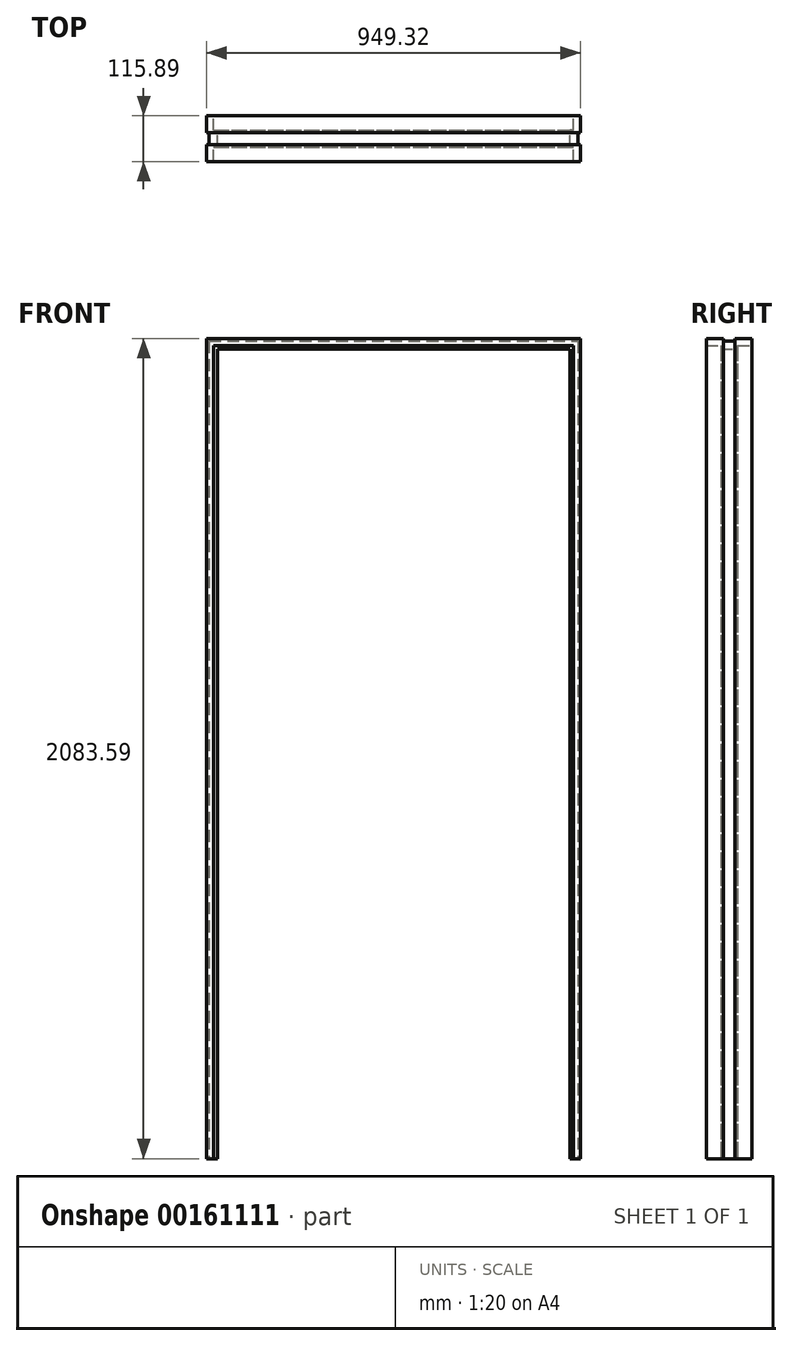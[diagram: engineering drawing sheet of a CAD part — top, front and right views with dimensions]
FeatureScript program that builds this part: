
annotation { "Feature Type Name" : "Feature", "Feature Type Description" : "" }
export const myFeature = defineFeature(function(context is Context, id is Id, definition is map)
    precondition{}
    {
        {
            var Q0;
            Q0=qCreatedBy(makeId("Top.planeOp"),FACE);
            var sketch = newSketch(context, id + "F0", { "sketchPlane" : qUnion([Q0])});
            skLineSegment(sketch, "E0", {"start": v(0, 115.89) * mm, "end": v(-17.46, 115.89) * mm});
            skLineSegment(sketch, "E1", {"start": v(-17.46, 115.89) * mm, "end": v(-17.46, 79.38) * mm});
            skLineSegment(sketch, "E2", {"start": v(-17.46, 79.38) * mm, "end": v(-26.99, 79.38) * mm});
            skLineSegment(sketch, "E3", {"start": v(-26.99, 79.38) * mm, "end": v(-26.99, 36.51) * mm});
            skLineSegment(sketch, "E4", {"start": v(-26.99, 36.51) * mm, "end": v(-17.46, 36.51) * mm});
            skLineSegment(sketch, "E5", {"start": v(-17.46, 36.51) * mm, "end": v(-17.46, 0) * mm});
            skLineSegment(sketch, "E6", {"start": v(-17.46, 0) * mm, "end": v(0, 0) * mm});
            skLineSegment(sketch, "E7", {"start": v(-474.66, 0) * mm, "end": v(-474.66, 102.45) * mm, "construction": true});
            skLineSegment(sketch, "E8.bottom", {"start": v(0, 73.03) * mm, "end": v(-6.35, 73.03) * mm});
            skLineSegment(sketch, "E8.top", {"start": v(0, 42.86) * mm, "end": v(-6.35, 42.86) * mm});
            skLineSegment(sketch, "E8.right", {"start": v(-6.35, 73.03) * mm, "end": v(-6.35, 42.86) * mm});
            skLineSegment(sketch, "E9", {"start": v(0, 115.89) * mm, "end": v(0, 73.03) * mm});
            skLineSegment(sketch, "E10", {"start": v(0, 42.86) * mm, "end": v(0, 0) * mm});
            skLineSegment(sketch, "E11.MirrorCS", {"start": v(-949.33, 73.03) * mm, "end": v(-942.98, 73.03) * mm});
            skLineSegment(sketch, "E12.MirrorCS", {"start": v(-949.33, 42.86) * mm, "end": v(-942.98, 42.86) * mm});
            skLineSegment(sketch, "E13.MirrorCS", {"start": v(-949.33, 115.89) * mm, "end": v(-931.86, 115.89) * mm});
            skLineSegment(sketch, "E14.MirrorCS", {"start": v(-931.86, 0) * mm, "end": v(-949.33, 0) * mm});
            skLineSegment(sketch, "E15.MirrorCS", {"start": v(-931.86, 79.38) * mm, "end": v(-922.34, 79.38) * mm});
            skLineSegment(sketch, "E16.MirrorCS", {"start": v(-922.34, 36.51) * mm, "end": v(-931.86, 36.51) * mm});
            skLineSegment(sketch, "E17.MirrorCS", {"start": v(-949.33, 42.86) * mm, "end": v(-949.33, 0) * mm});
            skLineSegment(sketch, "E18.MirrorCS", {"start": v(-949.33, 115.89) * mm, "end": v(-949.33, 73.03) * mm});
            skLineSegment(sketch, "E19.MirrorCS", {"start": v(-922.34, 79.38) * mm, "end": v(-922.34, 36.51) * mm});
            skLineSegment(sketch, "E20.MirrorCS", {"start": v(-931.86, 115.89) * mm, "end": v(-931.86, 79.38) * mm});
            skLineSegment(sketch, "E21.MirrorCS", {"start": v(-942.98, 73.03) * mm, "end": v(-942.98, 42.86) * mm});
            skLineSegment(sketch, "E22.MirrorCS", {"start": v(-931.86, 36.51) * mm, "end": v(-931.86, 0) * mm});
            skSolve(sketch);
        }
        {
            var Q0;
            Q0 = qSketchRegion(id + "F0", true);
            extrude(context, id + "F1", {"entities" : qUnion([Q0]), "depth" : 2083.6 * mm});
        }
        {
            var Q0;
            Q0=qCreatedBy(makeId("Front.planeOp"),FACE);
            var sketch = newSketch(context, id + "F2", { "sketchPlane" : qUnion([Q0])});
            skPoint(sketch, "E23.0", {"position": v(-949.33, 2083.6) * mm});
            skPoint(sketch, "E24.0", {"position": v(0, 2083.6) * mm});
            skLineSegment(sketch, "E25", {"start": v(-949.33, 2083.6) * mm, "end": v(-474.66, 1608.93) * mm});
            skLineSegment(sketch, "E26", {"start": v(-474.66, 1608.93) * mm, "end": v(0, 2083.6) * mm});
            skLineSegment(sketch, "E27", {"start": v(-949.33, 2083.6) * mm, "end": v(0, 2083.6) * mm});
            skSolve(sketch);
        }
        {
            var Q0;
            Q0 = qSketchRegion(id + "F2", true);
            extrude(context, id + "F3", {"entities" : qUnion([Q0]), "operationType" : NewBodyOperationType.REMOVE, "endBound" : BoundingType.THROUGH_ALL, "oppositeDirection" : true, "depth" : 25.4 * mm});
        }
        {
            var Q0;
            Q0=qCreatedBy(makeId("Right.planeOp"),FACE);
            var sketch = newSketch(context, id + "F4", { "sketchPlane" : qUnion([Q0])});
            skLineSegment(sketch, "E28.0.0", {"start": v(115.89, 2066.13) * mm, "end": v(79.38, 2066.13) * mm});
            skLineSegment(sketch, "E28.0.1", {"start": v(79.38, 2066.13) * mm, "end": v(79.38, 2056.6) * mm});
            skLineSegment(sketch, "E28.0.2", {"start": v(79.38, 2056.6) * mm, "end": v(36.51, 2056.6) * mm});
            skLineSegment(sketch, "E28.0.3", {"start": v(36.51, 2056.6) * mm, "end": v(36.51, 2066.13) * mm});
            skLineSegment(sketch, "E28.0.4", {"start": v(36.51, 2066.13) * mm, "end": v(0, 2066.13) * mm});
            skLineSegment(sketch, "E28.0.5", {"start": v(0, 2066.13) * mm, "end": v(0, 2083.6) * mm});
            skLineSegment(sketch, "E28.0.6", {"start": v(0, 2083.6) * mm, "end": v(42.86, 2083.6) * mm});
            skLineSegment(sketch, "E28.0.7", {"start": v(42.86, 2083.6) * mm, "end": v(42.86, 2077.24) * mm});
            skLineSegment(sketch, "E28.0.8", {"start": v(42.86, 2077.24) * mm, "end": v(73.03, 2077.24) * mm});
            skLineSegment(sketch, "E28.0.9", {"start": v(73.03, 2077.24) * mm, "end": v(73.03, 2083.6) * mm});
            skLineSegment(sketch, "E28.0.10", {"start": v(73.02, 2083.6) * mm, "end": v(115.89, 2083.6) * mm});
            skLineSegment(sketch, "E28.0.11", {"start": v(115.89, 2083.6) * mm, "end": v(115.89, 2066.13) * mm});
            skSolve(sketch);
        }
        {
            var Q0;
            Q0 = qSketchRegion(id + "F4", true);
            var Q1;
            Q1=makeQuery(id+"F1.opExtrude","SWEPT_FACE",FACE,{"disambiguationData":[OSD([sQuery(id+"F0.wireOp",EDGE,"E18.MirrorCS")])]});
            extrude(context, id + "F5", {"entities" : qUnion([Q0]), "operationType" : NewBodyOperationType.ADD, "endBound" : BoundingType.UP_TO_SURFACE, "oppositeDirection" : true, "endBoundEntityFace" : qUnion([Q1]), "depth" : 914.4 * mm});
        }
        {
            var Q0;
            Q0=qCreatedBy(makeId("Top.planeOp"),FACE);
            var sketch = newSketch(context, id + "F6", { "sketchPlane" : qUnion([Q0])});
            skLineSegment(sketch, "E29.0.0", {"start": v(-6.35, 73.03) * mm, "end": v(0, 73.03) * mm});
            skLineSegment(sketch, "E29.0.1", {"start": v(0, 73.03) * mm, "end": v(0, 42.86) * mm});
            skLineSegment(sketch, "E29.0.2", {"start": v(0, 42.86) * mm, "end": v(-6.35, 42.86) * mm});
            skLineSegment(sketch, "E29.0.3", {"start": v(-6.35, 42.86) * mm, "end": v(-6.35, 73.03) * mm});
            skLineSegment(sketch, "E30.0.0", {"start": v(-949.32, 42.86) * mm, "end": v(-949.32, 73.03) * mm});
            skLineSegment(sketch, "E30.0.1", {"start": v(-949.32, 73.03) * mm, "end": v(-942.98, 73.03) * mm});
            skLineSegment(sketch, "E30.0.2", {"start": v(-942.98, 73.03) * mm, "end": v(-942.98, 42.86) * mm});
            skLineSegment(sketch, "E30.0.3", {"start": v(-942.98, 42.86) * mm, "end": v(-949.32, 42.86) * mm});
            skSolve(sketch);
        }
        {
            var Q0;
            Q0 = qSketchRegion(id + "F6", true);
            extrude(context, id + "F7", {"entities" : qUnion([Q0]), "operationType" : NewBodyOperationType.REMOVE, "endBound" : BoundingType.THROUGH_ALL, "depth" : 25.4 * mm});
        }
    });
